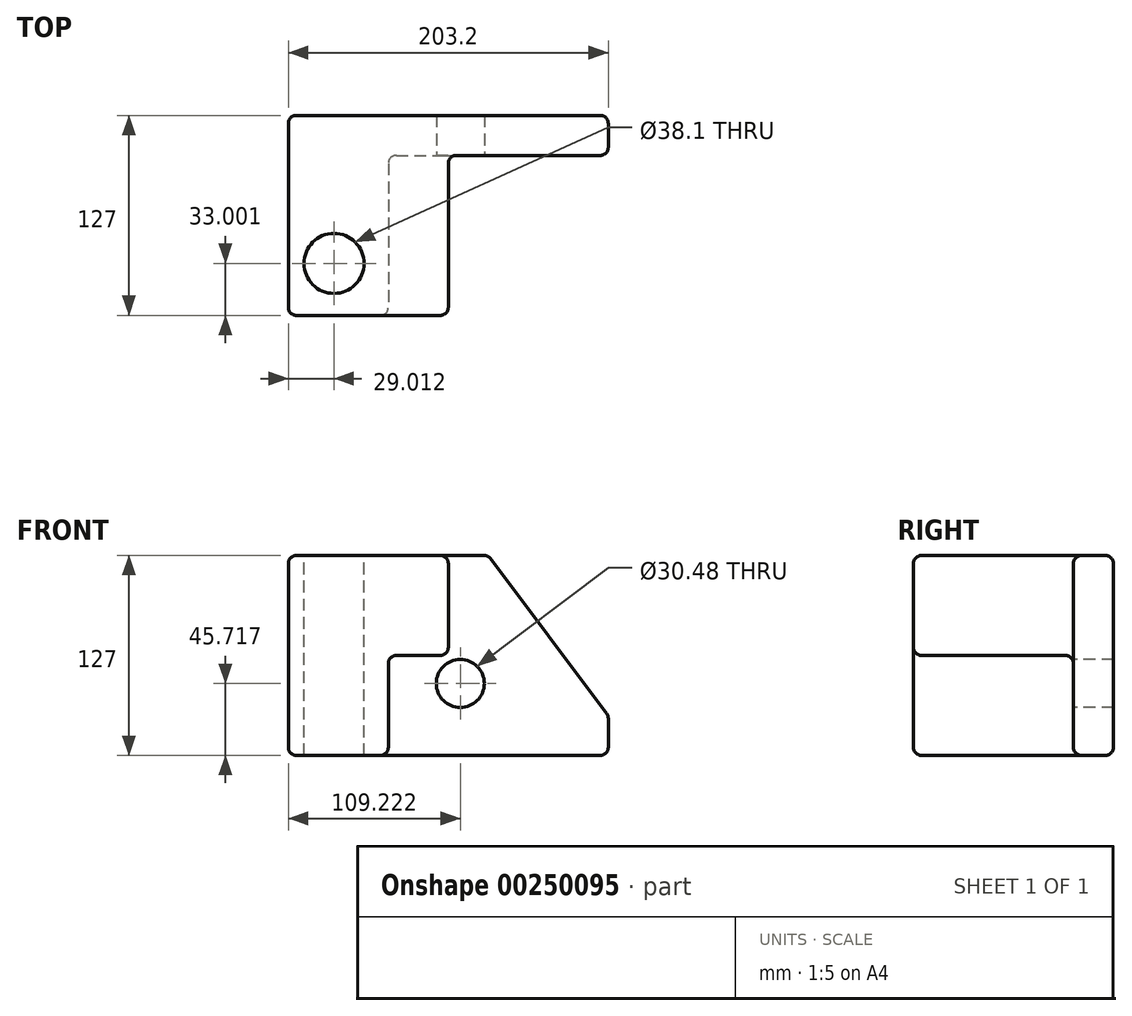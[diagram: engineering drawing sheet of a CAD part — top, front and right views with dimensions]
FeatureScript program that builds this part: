
annotation { "Feature Type Name" : "Feature", "Feature Type Description" : "" }
export const myFeature = defineFeature(function(context is Context, id is Id, definition is map)
    precondition{}
    {
        {
            var Q0;
            Q0=qCreatedBy(makeId("Front.planeOp"),FACE);
            var sketch = newSketch(context, id + "F0", { "sketchPlane" : qUnion([Q0])});
            skLineSegment(sketch, "E0.bottom", {"start": v(-110.03, 63.1) * mm, "end": v(93.17, 63.1) * mm});
            skLineSegment(sketch, "E0.top", {"start": v(-110.03, -63.9) * mm, "end": v(93.17, -63.9) * mm});
            skLineSegment(sketch, "E0.left", {"start": v(-110.03, 63.1) * mm, "end": v(-110.03, -63.9) * mm});
            skLineSegment(sketch, "E0.right", {"start": v(93.17, 63.1) * mm, "end": v(93.17, -63.9) * mm});
            skSolve(sketch);
        }
        {
            var Q0;
            Q0=makeQuery(id+"F0.imprint","IMPRINT",FACE,{"disambiguationData":[TD([[makeQuery(id+"F0.imprint","IMPRINT",EDGE,{"derivedFrom":sQuery(id+"F0.wireOp",EDGE,"E0.bottom")}),-1.0]])]});
            extrude(context, id + "F1", {"entities" : qUnion([Q0]), "depth" : 127 * mm});
        }
        {
            var Q0;
            Q0=makeQuery(id+"F1.opExtrude","CAP_FACE",FACE,{"disambiguationData":[OSD([sQuery(id+"F0.wireOp",EDGE,"E0.bottom"),sQuery(id+"F0.wireOp",EDGE,"E0.top"),sQuery(id+"F0.wireOp",EDGE,"E0.left"),sQuery(id+"F0.wireOp",EDGE,"E0.right")])],"isStart":false});
            var sketch = newSketch(context, id + "F2", { "sketchPlane" : qUnion([Q0])});
            skLineSegment(sketch, "E1.top", {"start": v(-110.03, -63.9) * mm, "end": v(-46.53, -63.9) * mm});
            skLineSegment(sketch, "E1.left", {"start": v(-110.03, 63.1) * mm, "end": v(-110.03, -63.9) * mm});
            skLineSegment(sketch, "E2", {"start": v(-46.53, -0.4) * mm, "end": v(-8.43, -0.4) * mm});
            skLineSegment(sketch, "E3", {"start": v(-8.43, -0.4) * mm, "end": v(-8.43, 63.1) * mm});
            skLineSegment(sketch, "E4", {"start": v(-46.53, -0.4) * mm, "end": v(-46.53, -63.9) * mm});
            skLineSegment(sketch, "E5", {"start": v(-110.03, -63.9) * mm, "end": v(-110.03, 63.1) * mm});
            skLineSegment(sketch, "E6", {"start": v(-110.03, 63.1) * mm, "end": v(-8.43, 63.1) * mm});
            skSolve(sketch);
        }
        {
            var Q0;
            Q0=makeQuery(id+"F2.imprint","IMPRINT",FACE,{"disambiguationData":[TD([[makeQuery(id+"F2.imprint","IMPRINT",EDGE,{"derivedFrom":sQuery(id+"F2.wireOp",EDGE,"E2")}),-1.0]])]});
            extrude(context, id + "F3", {"entities" : qUnion([Q0]), "operationType" : NewBodyOperationType.REMOVE, "oppositeDirection" : true, "depth" : 101.6 * mm});
        }
        {
            var Q0;
            Q0=makeQuery(id+"F1.opExtrude","SWEPT_EDGE",EDGE,{"disambiguationData":[OSD([sQuery(id+"F0.wireOp",EDGE,"E0.bottom"),sQuery(id+"F0.wireOp",EDGE,"E0.right")])]});
            chamfer(context, id + "F4", {"entities" : qUnion([Q0]), "chamferType" : ChamferType.TWO_OFFSETS, "width1" : 76.2 * mm, "oppositeDirection" : false, "width2" : 101.6 * mm, "tangentPropagation" : true});
        }
        {
            var Q0;
            Q0=makeQuery(id+"F1.opExtrude","SWEPT_FACE",FACE,{"disambiguationData":[OSD([sQuery(id+"F0.wireOp",EDGE,"E0.bottom")])]});
            var Q1;
            Q1=makeQuery(id+"F1.opExtrude","CAP_FACE",FACE,{"disambiguationData":[OSD([sQuery(id+"F0.wireOp",EDGE,"E0.bottom"),sQuery(id+"F0.wireOp",EDGE,"E0.top"),sQuery(id+"F0.wireOp",EDGE,"E0.left"),sQuery(id+"F0.wireOp",EDGE,"E0.right")])],"isStart":false});
            var Q2;
            Q2=makeQuery(id+"F3.boolean.opBoolean","COPY",FACE,{"derivedFrom":makeQuery(id+"F3.opExtrude","SWEPT_FACE",FACE,{"disambiguationData":[OSD([sQuery(id+"F2.wireOp",EDGE,"E3")])]})});
            var Q3;
            Q3=makeQuery(id+"F3.boolean.opBoolean","COPY",FACE,{"derivedFrom":makeQuery(id+"F3.opExtrude","SWEPT_FACE",FACE,{"disambiguationData":[OSD([sQuery(id+"F2.wireOp",EDGE,"E4")])]})});
            var Q4;
            Q4=makeQuery(id+"F3.boolean.opBoolean","COPY",FACE,{"derivedFrom":makeQuery(id+"F3.opExtrude","CAP_FACE",FACE,{"disambiguationData":[OSD([sQuery(id+"F0.wireOp",EDGE,"E0.bottom"),sQuery(id+"F0.wireOp",EDGE,"E0.top"),sQuery(id+"F0.wireOp",EDGE,"E0.right"),sQuery(id+"F2.wireOp",EDGE,"E2"),sQuery(id+"F2.wireOp",EDGE,"E3"),sQuery(id+"F2.wireOp",EDGE,"E4")])],"isStart":false})});
            var Q5;
            Q5=makeQuery(id+"F4.opChamfer","BLEND_FACE",FACE,{"disambiguationData":[OSD([sQuery(id+"F0.wireOp",EDGE,"E0.bottom"),sQuery(id+"F0.wireOp",EDGE,"E0.right")])]});
            var Q6;
            Q6=makeQuery(id+"F1.opExtrude","SWEPT_FACE",FACE,{"disambiguationData":[OSD([sQuery(id+"F0.wireOp",EDGE,"E0.right")])]});
            var Q7;
            Q7=makeQuery(id+"F1.opExtrude","SWEPT_FACE",FACE,{"disambiguationData":[OSD([sQuery(id+"F0.wireOp",EDGE,"E0.left")])]});
            var Q8;
            Q8=makeQuery(id+"F1.opExtrude","SWEPT_FACE",FACE,{"disambiguationData":[OSD([sQuery(id+"F0.wireOp",EDGE,"E0.top")])]});
            var Q9;
            Q9=makeQuery(id+"F1.opExtrude","CAP_FACE",FACE,{"disambiguationData":[OSD([sQuery(id+"F0.wireOp",EDGE,"E0.bottom"),sQuery(id+"F0.wireOp",EDGE,"E0.top"),sQuery(id+"F0.wireOp",EDGE,"E0.left"),sQuery(id+"F0.wireOp",EDGE,"E0.right")])],"isStart":true});
            fillet(context, id + "F5", {"entities" : qUnion([Q0, Q1, Q2, Q3, Q4, Q5, Q6, Q7, Q8, Q9]), "radius" : 5.08 * mm, "tangentPropagation" : true, "allowEdgeOverflow" : false});
        }
        {
            var Q0;
            Q0=makeQuery(id+"F3.boolean.opBoolean","COPY",FACE,{"derivedFrom":makeQuery(id+"F3.opExtrude","CAP_FACE",FACE,{"disambiguationData":[OSD([sQuery(id+"F0.wireOp",EDGE,"E0.bottom"),sQuery(id+"F0.wireOp",EDGE,"E0.top"),sQuery(id+"F0.wireOp",EDGE,"E0.right"),sQuery(id+"F2.wireOp",EDGE,"E2"),sQuery(id+"F2.wireOp",EDGE,"E3"),sQuery(id+"F2.wireOp",EDGE,"E4")])],"isStart":false})});
            var sketch = newSketch(context, id + "F6", { "sketchPlane" : qUnion([Q0])});
            skCircle(sketch, "E7", {"center": v(-0.8, -18.18) * mm, "radius": 15.24 * mm});
            skSolve(sketch);
        }
        {
            var Q0;
            Q0=makeQuery(id+"F6.imprint","IMPRINT",FACE,{"disambiguationData":[TD([[makeQuery(id+"F6.imprint","IMPRINT",EDGE,{"derivedFrom":sQuery(id+"F6.wireOp",EDGE,"E7")}),1.0]])]});
            extrude(context, id + "F7", {"entities" : qUnion([Q0]), "operationType" : NewBodyOperationType.REMOVE, "endBound" : BoundingType.UP_TO_NEXT, "oppositeDirection" : true, "depth" : 25.4 * mm});
        }
        {
            var Q0;
            Q0=makeQuery(id+"F1.opExtrude","SWEPT_FACE",FACE,{"disambiguationData":[OSD([sQuery(id+"F0.wireOp",EDGE,"E0.bottom")])]});
            var sketch = newSketch(context, id + "F8", { "sketchPlane" : qUnion([Q0])});
            skCircle(sketch, "E8", {"center": v(-81.02, -94) * mm, "radius": 19.05 * mm});
            skSolve(sketch);
        }
        {
            var Q0;
            Q0=makeQuery(id+"F8.imprint","IMPRINT",FACE,{"disambiguationData":[TD([[makeQuery(id+"F8.imprint","IMPRINT",EDGE,{"derivedFrom":sQuery(id+"F8.wireOp",EDGE,"E8")}),1.0]])]});
            extrude(context, id + "F9", {"entities" : qUnion([Q0]), "operationType" : NewBodyOperationType.REMOVE, "endBound" : BoundingType.UP_TO_NEXT, "oppositeDirection" : true, "depth" : 25.4 * mm});
        }
    });
